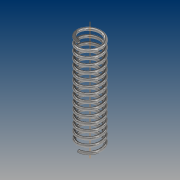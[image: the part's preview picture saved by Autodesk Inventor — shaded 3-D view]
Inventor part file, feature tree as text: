
AUTODESK INVENTOR PART (.ipt)
format: ipt  version: 2021 (Build 250183000, 183)  size: 348,160 bytes
history: native  units: mm
features: sketch x2, extrude x1, helix x1
ambient origin geometry x8: Origin, YZ Plane, XZ Plane, XY Plane, X Axis, Y Axis, Z Axis, Center Point
bodies: Solid1 (feature_tree)
feature tree (4):
  sketch  "Sketch1"  dims[d0=1.36mm d1=5.3mm d2=45.0mm d3=0.0mm]
  extrude  "Extrusion1"  Depth=5.3mm
  helix  "Coil1"  [1 undecoded]
  sketch  "Sketch2"  dims[d4=3.0mm d5=45.0mm d6=10.0mm d7=0.0mm d8=90.0deg d9=90.0deg d10=0.0mm d11=0.0mm]
note: 1 required parameter value undecoded (feature->parameter linkage not recoverable at this tier; creation-order binding heuristic only, values carry confidence <= 0.55)
